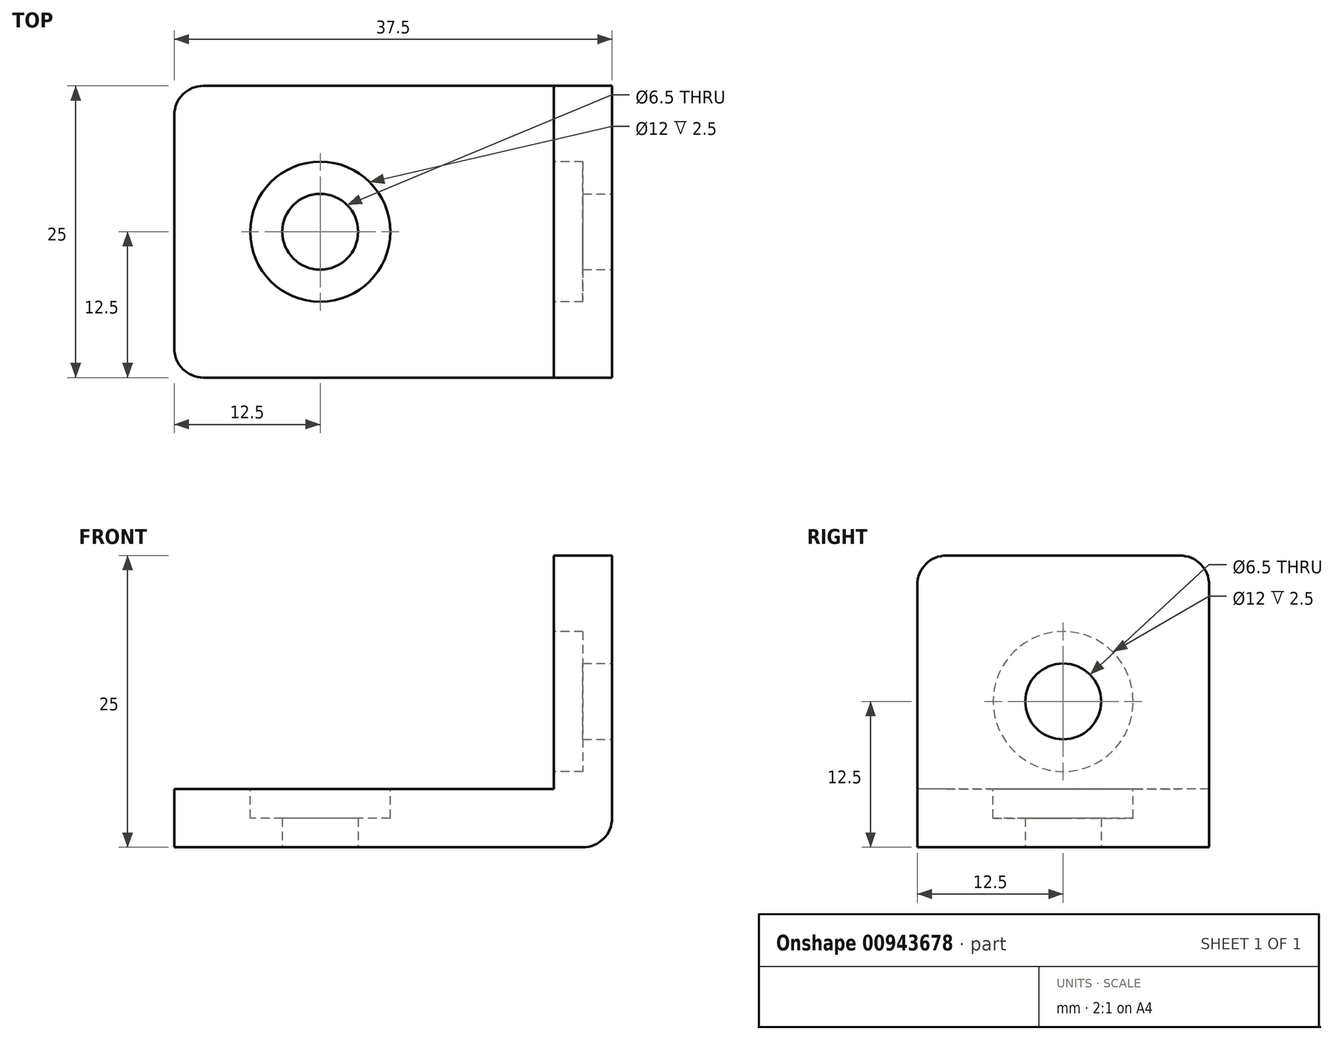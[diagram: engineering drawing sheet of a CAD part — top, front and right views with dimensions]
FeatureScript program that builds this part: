
annotation { "Feature Type Name" : "Feature", "Feature Type Description" : "" }
export const myFeature = defineFeature(function(context is Context, id is Id, definition is map)
    precondition{}
    {
        {
            var Q0;
            Q0=qCreatedBy(makeId("Top.planeOp"),FACE);
            var sketch = newSketch(context, id + "F0", { "sketchPlane" : qUnion([Q0])});
            skCircle(sketch, "E0", {"center": v(0, 0) * mm, "radius": 3.25 * mm});
            skLineSegment(sketch, "E1.bottom", {"start": v(12.5, -12.5) * mm, "end": v(-12.5, -12.5) * mm});
            skLineSegment(sketch, "E1.top", {"start": v(12.5, 12.5) * mm, "end": v(-12.5, 12.5) * mm});
            skLineSegment(sketch, "E1.left", {"start": v(12.5, -12.5) * mm, "end": v(12.5, 12.5) * mm});
            skLineSegment(sketch, "E1.right", {"start": v(-12.5, -12.5) * mm, "end": v(-12.5, 12.5) * mm});
            skLineSegment(sketch, "E2.bottom", {"start": v(12.5, 12.5) * mm, "end": v(25, 12.5) * mm});
            skLineSegment(sketch, "E2.top", {"start": v(12.5, -12.5) * mm, "end": v(25, -12.5) * mm});
            skLineSegment(sketch, "E2.left", {"start": v(12.5, 12.5) * mm, "end": v(12.5, -12.5) * mm});
            skLineSegment(sketch, "E2.right", {"start": v(25, 12.5) * mm, "end": v(25, -12.5) * mm});
            skSolve(sketch);
        }
        {
            var Q0;
            Q0 = qSketchRegion(id + "F0", true);
            extrude(context, id + "F1", {"entities" : qUnion([Q0]), "depth" : 5 * mm, "offsetDistance" : 25 * mm});
        }
        {
            var Q0;
            Q0=makeQuery(id+"F1.opExtrude","CAP_FACE",FACE,{"disambiguationData":[OSD([sQuery(id+"F0.wireOp",EDGE,"E0"),sQuery(id+"F0.wireOp",EDGE,"E1.bottom"),sQuery(id+"F0.wireOp",EDGE,"E1.top"),sQuery(id+"F0.wireOp",EDGE,"E1.right"),sQuery(id+"F0.wireOp",EDGE,"E2.bottom"),sQuery(id+"F0.wireOp",EDGE,"E2.top"),sQuery(id+"F0.wireOp",EDGE,"E2.right")])],"isStart":false});
            var sketch = newSketch(context, id + "F2", { "sketchPlane" : qUnion([Q0])});
            skCircle(sketch, "E3", {"center": v(0, 0) * mm, "radius": 6 * mm});
            skSolve(sketch);
        }
        {
            var Q0;
            Q0 = qSketchRegion(id + "F2", true);
            extrude(context, id + "F3", {"entities" : qUnion([Q0]), "operationType" : NewBodyOperationType.REMOVE, "oppositeDirection" : true, "depth" : 2.5 * mm, "offsetDistance" : 25 * mm});
        }
        {
            var Q0;
            Q0=makeQuery(id+"F1.opExtrude","CAP_FACE",FACE,{"disambiguationData":[OSD([sQuery(id+"F0.wireOp",EDGE,"E0"),sQuery(id+"F0.wireOp",EDGE,"E1.bottom"),sQuery(id+"F0.wireOp",EDGE,"E1.top"),sQuery(id+"F0.wireOp",EDGE,"E1.right"),sQuery(id+"F0.wireOp",EDGE,"E2.bottom"),sQuery(id+"F0.wireOp",EDGE,"E2.top"),sQuery(id+"F0.wireOp",EDGE,"E2.right")])],"isStart":false});
            var sketch = newSketch(context, id + "F4", { "sketchPlane" : qUnion([Q0])});
            skLineSegment(sketch, "E4.bottom", {"start": v(25, 12.5) * mm, "end": v(20, 12.5) * mm});
            skLineSegment(sketch, "E4.top", {"start": v(25, -12.5) * mm, "end": v(20, -12.5) * mm});
            skLineSegment(sketch, "E4.left", {"start": v(25, 12.5) * mm, "end": v(25, -12.5) * mm});
            skLineSegment(sketch, "E4.right", {"start": v(20, 12.5) * mm, "end": v(20, -12.5) * mm});
            skSolve(sketch);
        }
        {
            var Q0;
            Q0=makeQuery(id+"F4.imprint","IMPRINT",FACE,{"disambiguationData":[TD([[makeQuery(id+"F4.imprint","IMPRINT",EDGE,{"derivedFrom":sQuery(id+"F4.wireOp",EDGE,"E4.bottom")}),-1.0]])]});
            extrude(context, id + "F5", {"entities" : qUnion([Q0]), "operationType" : NewBodyOperationType.ADD, "depth" : 20 * mm, "offsetDistance" : 25 * mm});
        }
        {
            var Q0;
            Q0=makeQuery(id+"F5.boolean.opBoolean","MERGE",FACE,{"derivedFrom":[makeQuery(id+"F1.opExtrude","SWEPT_FACE",FACE,{"disambiguationData":[OSD([sQuery(id+"F0.wireOp",EDGE,"E2.right")])]}),makeQuery(id+"F5.opExtrude","SWEPT_FACE",FACE,{"disambiguationData":[OSD([sQuery(id+"F4.wireOp",EDGE,"E4.left")])]})]});
            var sketch = newSketch(context, id + "F6", { "sketchPlane" : qUnion([Q0])});
            skLineSegment(sketch, "E5", {"start": v(0, 25) * mm, "end": v(0, 0) * mm, "construction": true});
            skCircle(sketch, "E6", {"center": v(0, 12.5) * mm, "radius": 3.25 * mm});
            skSolve(sketch);
        }
        {
            var Q0;
            Q0=makeQuery(id+"F6.imprint","IMPRINT",FACE,{"disambiguationData":[TD([[makeQuery(id+"F6.imprint","IMPRINT",EDGE,{"derivedFrom":sQuery(id+"F6.wireOp",EDGE,"E6")}),1.0]])]});
            extrude(context, id + "F7", {"entities" : qUnion([Q0]), "operationType" : NewBodyOperationType.REMOVE, "oppositeDirection" : true, "depth" : 25 * mm, "offsetDistance" : 25 * mm});
        }
        {
            var Q0;
            Q0=makeQuery(id+"F5.opExtrude","SWEPT_FACE",FACE,{"disambiguationData":[OSD([sQuery(id+"F4.wireOp",EDGE,"E4.right")])]});
            var sketch = newSketch(context, id + "F8", { "sketchPlane" : qUnion([Q0])});
            skCircle(sketch, "E7", {"center": v(0, 12.5) * mm, "radius": 6 * mm});
            skSolve(sketch);
        }
        {
            var Q0;
            Q0=makeQuery(id+"F8.imprint","IMPRINT",FACE,{"disambiguationData":[TD([[makeQuery(id+"F8.imprint","IMPRINT",EDGE,{"derivedFrom":sQuery(id+"F8.wireOp",EDGE,"E7")}),1.0]])]});
            extrude(context, id + "F9", {"entities" : qUnion([Q0]), "operationType" : NewBodyOperationType.REMOVE, "oppositeDirection" : true, "depth" : 2.5 * mm, "offsetDistance" : 25 * mm});
        }
        {
            var Q0;
            Q0=makeQuery(id+"F5.opExtrude","CAP_EDGE",EDGE,{"disambiguationData":[OSD([sQuery(id+"F4.wireOp",EDGE,"E4.right")])],"isStart":true});
            var Q1;
            Q1=makeQuery(id+"F1.opExtrude","CAP_EDGE",EDGE,{"disambiguationData":[OSD([sQuery(id+"F0.wireOp",EDGE,"E2.right")])],"isStart":true});
            var Q2;
            Q2=makeQuery(id+"F1.opExtrude","SWEPT_EDGE",EDGE,{"disambiguationData":[OSD([sQuery(id+"F0.wireOp",EDGE,"E1.bottom"),sQuery(id+"F0.wireOp",EDGE,"E1.right")])]});
            var Q3;
            Q3=makeQuery(id+"F1.opExtrude","SWEPT_EDGE",EDGE,{"disambiguationData":[OSD([sQuery(id+"F0.wireOp",EDGE,"E1.top"),sQuery(id+"F0.wireOp",EDGE,"E1.right")])]});
            var Q4;
            Q4=makeQuery(id+"F5.opExtrude","CAP_EDGE",EDGE,{"disambiguationData":[OSD([sQuery(id+"F4.wireOp",EDGE,"E4.top")])],"isStart":false});
            var Q5;
            Q5=makeQuery(id+"F5.opExtrude","CAP_EDGE",EDGE,{"disambiguationData":[OSD([sQuery(id+"F4.wireOp",EDGE,"E4.bottom")])],"isStart":false});
            fillet(context, id + "F10", {"entities" : qUnion([Q0, Q1, Q2, Q3, Q4, Q5]), "tangentPropagation" : true, "radius" : 2.5 * mm, "defaultsChanged" : false, "vertexSettings" : [], "allowEdgeOverflow" : false});
        }
    });
